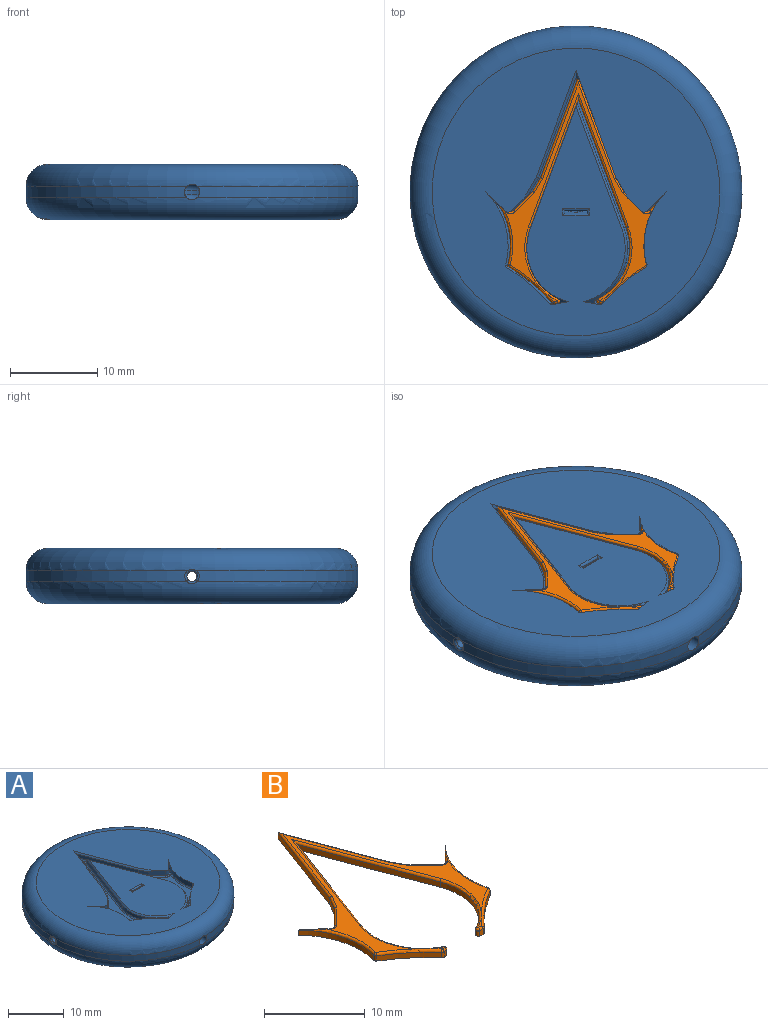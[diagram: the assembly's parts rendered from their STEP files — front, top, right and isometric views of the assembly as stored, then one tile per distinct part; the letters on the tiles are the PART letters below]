
ASSEMBLY  parts=2 mates=1
PART A: 133 faces, bbox 41.4x41.4x6.5 mm
  f0: cylinder r=19.05mm len=38.09mm, axis (0,0,-1), area 74.1mm2, adj f71,f72,f127,f131
  f1: cylinder r=19.05mm len=18.57mm, axis (0,0,-1), area 36mm2, adj f71,f72,f73,f126
  f2: cylinder r=2.31mm len=0.5mm, axis (0,0,1), area 0.1mm2, adj f92,f95,f97,f118
  f3: cylinder r=2.31mm len=0.5mm, axis (0,0,1), area 0.1mm2, adj f89,f95,f103,f111
  f4: cylinder r=0.57mm len=16.02mm, axis (1,0,0), area 56.8mm2, adj f105,f108,f109,f110,f111,f112,f125,f126
  f5: cylinder r=0.57mm len=16.02mm, axis (1,0,0), area 56.8mm2, adj f113,f116,f117,f118,f119,f120,f129,f130
  f6: plane 1.28x0.89mm, normal (0,0,1), area 0.2mm2, adj f49,f51,f54
  f7: plane 1.28x0.89mm, normal (0,0,1), area 0.2mm2, adj f60,f62,f65
  f8: plane 33.02x33.02mm, normal (0,0,1), area 758.2mm2, adj f10,f11,f12,f13,f18,f19,f20,f21
  f9: cylinder r=19.05mm len=18.57mm, axis (0,0,-1), area 36mm2, adj f71,f72,f73,f130
  f10: plane 2.17x2.17mm, normal (-0.71,-0.71,0), area 3.1mm2, adj f8,f11,f29,f61
  f11: cylinder r=8.72mm len=8.39mm, axis (0,0,1), area 9.2mm2, adj f8,f10,f35,f64
  f12: cylinder r=19.61mm len=4.97mm, axis (0,0,1), area 6.6mm2, adj f8,f35,f36,f65
  f13: plane 2.06x1.13mm, normal (-0.16,0.99,0), area 1mm2, adj f8,f34,f36,f37,f60
  f14: cylinder r=6.59mm len=8.22mm, axis (0,0,1), area 7.4mm2, adj f15,f34,f37,f62
  f15: plane 14.68x5.49mm, normal (-0.94,0.35,0), area 11.9mm2, adj f14,f16,f33,f58
  f16: plane 14.68x5.49mm, normal (0.94,0.35,0), area 11.9mm2, adj f15,f17,f32,f56
  f17: cylinder r=6.59mm len=8.22mm, axis (0,0,1), area 7.4mm2, adj f16,f31,f38,f54
  f18: plane 2.06x1.13mm, normal (0.16,0.99,0), area 1mm2, adj f8,f31,f38,f39,f49
  f19: cylinder r=19.61mm len=4.97mm, axis (0,0,1), area 6.6mm2, adj f8,f39,f40,f51
  f20: cylinder r=8.72mm len=8.39mm, axis (0,0,1), area 9.2mm2, adj f8,f21,f40,f45
  f21: plane 2.17x2.17mm, normal (0.71,-0.71,0), area 3.1mm2, adj f8,f20,f22,f43
  f22: cylinder r=0.53mm len=1.02mm, axis (0,0,1), area 0.8mm2, adj f8,f21,f23,f41
  f23: plane 2.17x2.17mm, normal (-0.71,-0.71,0), area 3mm2, adj f8,f22,f24,f42,f67
  f24: plane 1.58x0.92mm, normal (-0.86,-0.5,0), area 1.4mm2, adj f23,f25,f44,f67
  f25: plane 11.6x4.33mm, normal (-0.94,-0.35,0), area 9.4mm2, adj f24,f26,f46,f68
  f26: plane 11.6x4.33mm, normal (0.94,-0.35,0), area 9.4mm2, adj f25,f27,f50,f70
  f27: plane 1.58x0.92mm, normal (0.86,-0.5,0), area 1.4mm2, adj f26,f28,f53,f69
  f28: plane 2.17x2.17mm, normal (0.71,-0.71,0), area 3mm2, adj f8,f27,f29,f55,f69
  f29: cylinder r=0.53mm len=1.02mm, axis (0,0,1), area 0.8mm2, adj f8,f10,f28,f57
  f30: plane 23.34x16.83mm, normal (0,0,1), area 44mm2, adj f41,f42,f43,f44,f45,f46,f50,f51
  f31: cone r=6.59mm half-angle=45deg, axis (0,0,-1), area 4.1mm2, adj f8,f17,f18,f32,f38
  f32: plane 14.77x5.49mm, normal (0.66,0.25,0.71), area 5.5mm2, adj f8,f16,f31,f33
  f33: plane 14.77x5.49mm, normal (-0.66,0.25,0.71), area 5.5mm2, adj f8,f15,f32,f34
  f34: cone r=6.33mm half-angle=45deg, axis (0,0,-1), area 4.1mm2, adj f8,f13,f14,f33,f37
  f35: cylinder r=0.25mm len=1.02mm, axis (0,0,-1), area 0.3mm2, adj f8,f11,f12,f66
  f36: cylinder r=0.25mm len=1.02mm, axis (0,0,1), area 0.3mm2, adj f8,f12,f13,f63
  f37: cylinder r=0.25mm len=0.76mm, axis (0,0,1), area 0.3mm2, adj f13,f14,f34,f59
  f38: cylinder r=0.25mm len=0.76mm, axis (0,0,1), area 0.3mm2, adj f17,f18,f31,f52
  f39: cylinder r=0.25mm len=1.02mm, axis (0,0,1), area 0.3mm2, adj f8,f18,f19,f48
  f40: cylinder r=0.25mm len=1.02mm, axis (0,0,-1), area 0.3mm2, adj f8,f19,f20,f47
  f41: torus R=0.78mm, axis (0,0,1), area 0.4mm2, adj f22,f30,f42,f43
  f42: cylinder r=0.25mm len=2.37mm, axis (-0.71,0.71,0), area 1.2mm2, adj f23,f30,f41,f44
  f43: cylinder r=0.25mm len=2.35mm, axis (-0.71,-0.71,0), area 0.6mm2, adj f21,f30,f41,f45
  f44: cylinder r=0.25mm len=1.75mm, axis (-0.5,0.86,0), area 0.7mm2, adj f24,f30,f42,f46
  f45: torus R=8.97mm, axis (0,0,1), area 3.1mm2, adj f20,f30,f43,f47
  f46: cylinder r=0.25mm len=11.71mm, axis (-0.35,0.94,0), area 4.8mm2, adj f25,f30,f44,f50
  f47: sphere r=0.25mm, area 0.1mm2, adj f40,f45,f51
  f48: sphere r=0.25mm, area 0.1mm2, adj f39,f49,f51
  f49: cylinder r=0.25mm len=0.51mm, axis (0.99,-0.16,0), area 0.2mm2, adj f6,f18,f48,f52
  f50: cylinder r=0.25mm len=11.71mm, axis (-0.35,-0.94,0), area 4.8mm2, adj f26,f30,f46,f53
  f51: torus R=19.87mm, axis (0,0,1), area 2.6mm2, adj f6,f19,f30,f47,f48,f54
  f52: sphere r=0.25mm, area 0.2mm2, adj f38,f49,f54
  f53: cylinder r=0.25mm len=1.75mm, axis (-0.5,-0.86,0), area 0.7mm2, adj f27,f30,f50,f55
  f54: torus R=6.84mm, axis (0,0,1), area 3.9mm2, adj f6,f17,f30,f51,f52,f56
  f55: cylinder r=0.25mm len=2.37mm, axis (-0.71,-0.71,0), area 1.2mm2, adj f28,f30,f53,f57
  f56: cylinder r=0.25mm len=15.41mm, axis (0.35,-0.94,0), area 6.4mm2, adj f16,f30,f54,f58
  f57: torus R=0.78mm, axis (0,0,1), area 0.4mm2, adj f29,f30,f55,f61
  f58: cylinder r=0.25mm len=15.41mm, axis (0.35,0.94,0), area 6.4mm2, adj f15,f30,f56,f62
  f59: sphere r=0.25mm, area 0.1mm2, adj f37,f60,f62
  f60: cylinder r=0.25mm len=0.51mm, axis (0.99,0.16,0), area 0.2mm2, adj f7,f13,f59,f63
  f61: cylinder r=0.25mm len=2.35mm, axis (-0.71,0.71,0), area 0.6mm2, adj f10,f30,f57,f64
  f62: torus R=6.84mm, axis (0,0,1), area 3.9mm2, adj f7,f14,f30,f58,f59,f65
  f63: sphere r=0.25mm, area 0.1mm2, adj f36,f60,f65
  f64: torus R=8.97mm, axis (0,0,1), area 3.1mm2, adj f11,f30,f61,f66
  f65: torus R=19.87mm, axis (0,0,1), area 2.6mm2, adj f7,f12,f30,f62,f63,f66
  f66: sphere r=0.25mm, area 0.1mm2, adj f35,f64,f65
  f67: plane 2.4x1.63mm, normal (-0.61,-0.36,0.71), area 0.8mm2, adj f8,f23,f24,f68
  f68: plane 12.32x4.56mm, normal (-0.66,-0.25,0.71), area 4.6mm2, adj f8,f25,f67,f70
  f69: plane 2.4x1.63mm, normal (0.61,-0.36,0.71), area 0.8mm2, adj f8,f27,f28,f70
  f70: plane 12.32x4.56mm, normal (0.66,-0.25,0.71), area 4.6mm2, adj f8,f26,f68,f69
  f71: torus R=16.51mm, axis (0,0,1), area 453.9mm2, adj f0,f1,f9,f73,f87,f128,f129
  f72: torus R=16.51mm, axis (0,0,1), area 454mm2, adj f0,f1,f8,f9,f73,f125,f132
  f73: cylinder r=0.89mm len=16.69mm, axis (0,-1,0), area 85.5mm2, adj f1,f9,f71,f72,f77,f96,f97,f98
  f74: cylinder r=2.31mm len=3.97mm, axis (0,0,1), area 2.4mm2, adj f93,f95,f110,f119
  f75: plane 3.56x3.28mm, normal (0,0,-1), area 9.6mm2, adj f82,f83,f84,f95
  f76: plane 3.69x3.47mm, normal (0,0,1), area 8.7mm2, adj f89,f90,f91,f92,f93,f94
  f77: cylinder r=0.51mm len=2.54mm, axis (1,0,0), area 1.2mm2, adj f73,f78,f79,f83,f84,f85,f96,f104
  f78: plane 0.19x0.13mm, normal (0,0.24,0.97), area 0mm2, adj f77,f80,f83,f96
  f79: plane 0.19x0.13mm, normal (0,0.24,0.97), area 0mm2, adj f77,f81,f84,f104
  f80: plane 0.07x0.05mm, normal (0,0,1), area 0mm2, adj f78,f83,f96
  f81: plane 0.07x0.05mm, normal (0,0,1), area 0mm2, adj f79,f84,f104
  f82: cylinder r=0.51mm len=2.54mm, axis (1,0,0), area 1.4mm2, adj f75,f83,f84,f86
  f83: plane 2.34x1.46mm, normal (-1,0,0), area 0.7mm2, adj f75,f77,f78,f80,f82,f85,f86,f95
  f84: plane 2.34x1.46mm, normal (1,0,0), area 0.7mm2, adj f75,f77,f79,f81,f82,f85,f86,f95
  f85: plane 2.54x1.76mm, normal (0,1,0), area 4.5mm2, adj f77,f83,f84,f124
  f86: plane 2.54x1.58mm, normal (0,-1,0), area 4mm2, adj f82,f83,f84,f121
  f87: cylinder r=16.51mm len=33.02mm, axis (0,0,1), area 131.7mm2, adj f71,f88
  f88: plane 33.02x33.02mm, normal (0,0,-1), area 856.3mm2, adj f87
  f89: torus R=1.64mm, axis (0,0,1), area 1mm2, adj f3,f76,f90,f91,f102,f109
  f90: bspline ~1.73x0.82mm, area 0.2mm2, adj f76,f89,f92,f99,f100,f101
  f91: bspline ~1.08x0.73mm, area 0.4mm2, adj f76,f89,f93,f105,f106,f107
  f92: torus R=1.64mm, axis (0,0,1), area 1mm2, adj f2,f76,f90,f94,f98,f116
  f93: torus R=1.64mm, axis (0,0,1), area 5.4mm2, adj f74,f76,f91,f94,f108,f117
  f94: bspline ~1.08x0.73mm, area 0.4mm2, adj f76,f92,f93,f113,f114,f115
  f95: torus R=1.64mm, axis (0,0,1), area 7.6mm2, adj f2,f3,f74,f75,f83,f84,f96,f104
  f96: bspline ~3.04x1.8mm, area 2.7mm2, adj f73,f77,f78,f80,f83,f95,f97
  f97: bspline ~3.16x1.78mm, area 0.9mm2, adj f2,f73,f96,f98
  f98: bspline ~3.05x1.76mm, area 3.1mm2, adj f73,f92,f97,f99
  f99: bspline ~1.21x0.49mm, area 0.1mm2, adj f90,f98,f100
  f100: bspline ~0.82x0.48mm, area 0.3mm2, adj f73,f90,f99,f101
  f101: bspline ~1.29x0.58mm, area 0.3mm2, adj f73,f90,f100,f102
  f102: bspline ~3.05x1.76mm, area 3mm2, adj f73,f89,f101,f103
  f103: bspline ~3.17x2.53mm, area 0.9mm2, adj f3,f73,f102,f104
  f104: bspline ~3.04x1.8mm, area 2.7mm2, adj f73,f77,f79,f81,f84,f95,f103
  f105: bspline ~0.74x0.66mm, area 0.3mm2, adj f4,f91,f106,f107
  f106: bspline ~0.8x0.25mm, area 0mm2, adj f91,f105,f108
  f107: bspline ~0.8x0.25mm, area 0mm2, adj f91,f105,f109
  f108: bspline ~1.11x1.02mm, area 0.8mm2, adj f4,f93,f106,f110
  f109: bspline ~1.12x1.03mm, area 0.8mm2, adj f4,f89,f107,f111
  f110: bspline ~1.15x0.99mm, area 0.4mm2, adj f4,f74,f108,f112
  f111: bspline ~1.16x0.99mm, area 0.4mm2, adj f3,f4,f109,f112
  f112: bspline ~2.38x1.13mm, area 2.1mm2, adj f4,f95,f110,f111
  f113: bspline ~0.74x0.66mm, area 0.3mm2, adj f5,f94,f114,f115
  f114: bspline ~0.8x0.25mm, area 0mm2, adj f94,f113,f116
  f115: bspline ~0.8x0.25mm, area 0mm2, adj f94,f113,f117
  f116: bspline ~1.12x1.03mm, area 0.8mm2, adj f5,f92,f114,f118
  f117: bspline ~1.11x1.02mm, area 0.8mm2, adj f5,f93,f115,f119
  f118: bspline ~1.15x0.99mm, area 0.4mm2, adj f2,f5,f116,f120
  f119: bspline ~1.16x0.99mm, area 0.4mm2, adj f5,f74,f117,f120
  f120: bspline ~2.38x1.13mm, area 2.1mm2, adj f5,f95,f118,f119
  f121: cylinder r=0.25mm len=3.05mm, axis (1,0,0), area 1.1mm2, adj f8,f86,f122,f123
  f122: cylinder r=0.25mm len=0.76mm, axis (0,1,0), area 0.2mm2, adj f8,f84,f121,f124
  f123: cylinder r=0.25mm len=0.76mm, axis (0,-1,0), area 0.2mm2, adj f8,f83,f121,f124
  f124: cylinder r=0.25mm len=3.05mm, axis (-1,0,0), area 1.1mm2, adj f8,f85,f122,f123
  f125: bspline ~1.12x0.46mm, area 0.3mm2, adj f4,f72,f126,f127
  f126: bspline ~1.44x0.61mm, area 0.5mm2, adj f1,f4,f125,f128
  f127: bspline ~1.37x0.57mm, area 0.5mm2, adj f0,f4,f125,f128
  f128: bspline ~1.32x0.56mm, area 0.4mm2, adj f4,f71,f126,f127
  f129: bspline ~1.32x0.56mm, area 0.4mm2, adj f5,f71,f130,f131
  f130: bspline ~1.45x0.6mm, area 0.5mm2, adj f5,f9,f129,f132
  f131: bspline ~1.37x0.56mm, area 0.5mm2, adj f0,f5,f129,f132
  f132: bspline ~1.12x0.46mm, area 0.3mm2, adj f5,f72,f130,f131
PART B: 56 faces, bbox 21x26.4x0.9 mm
  f0: plane 1.23x0.89mm, normal (0,0,1), area 0.2mm2, adj f34,f35,f37,f51,f53
  f1: plane 1.23x0.89mm, normal (0,0,1), area 0.2mm2, adj f25,f26,f28,f47,f49
  f2: plane 23.34x16.83mm, normal (0,0,1), area 44mm2, adj f24,f25,f27,f28,f29,f30,f31,f32
  f3: cylinder r=19.61mm len=4.95mm, axis (0,0,1), area 4.1mm2, adj f23,f37,f52,f54
  f4: plane 0.64x0.38mm, normal (0.16,-0.99,0), area 0.2mm2, adj f23,f35,f50,f52
  f5: cylinder r=6.59mm len=8.19mm, axis (0,0,1), area 6.1mm2, adj f6,f23,f34,f50
  f6: plane 14.68x5.49mm, normal (0.94,-0.35,0), area 10mm2, adj f5,f7,f23,f32
  f7: plane 14.68x5.49mm, normal (-0.94,-0.35,0), area 10mm2, adj f6,f8,f23,f30
  f8: cylinder r=6.59mm len=8.19mm, axis (0,0,1), area 6.1mm2, adj f7,f23,f28,f48
  f9: plane 0.64x0.38mm, normal (-0.16,-0.99,0), area 0.2mm2, adj f23,f26,f46,f48
  f10: cylinder r=19.61mm len=4.95mm, axis (0,0,1), area 4.1mm2, adj f23,f25,f44,f46
  f11: cylinder r=8.72mm len=8.38mm, axis (0,0,1), area 5.8mm2, adj f12,f23,f24,f44
  f12: plane 2.17x2.17mm, normal (-0.71,0.71,0), area 2mm2, adj f11,f13,f23,f27
  f13: cylinder r=0.53mm len=0.75mm, axis (0,0,1), area 0.5mm2, adj f12,f14,f23,f29
  f14: plane 2.17x2.17mm, normal (0.71,0.71,0), area 1.9mm2, adj f13,f15,f23,f31
  f15: plane 1.58x0.92mm, normal (0.86,0.5,0), area 1.2mm2, adj f14,f16,f23,f33
  f16: plane 11.6x4.33mm, normal (0.94,0.35,0), area 7.9mm2, adj f15,f17,f23,f36
  f17: plane 11.6x4.33mm, normal (-0.94,0.35,0), area 7.9mm2, adj f16,f18,f23,f38
  f18: plane 1.58x0.92mm, normal (-0.86,0.5,0), area 1.2mm2, adj f17,f19,f23,f40
  f19: plane 2.17x2.17mm, normal (-0.71,0.71,0), area 1.9mm2, adj f18,f20,f23,f42
  f20: cylinder r=0.53mm len=0.75mm, axis (0,0,1), area 0.5mm2, adj f19,f21,f23,f43
  f21: plane 2.17x2.17mm, normal (0.71,0.71,0), area 2mm2, adj f20,f22,f23,f41
  f22: cylinder r=8.72mm len=8.38mm, axis (0,0,1), area 5.8mm2, adj f21,f23,f39,f54
  f23: plane 26.1x20.68mm, normal (0,0,-1), area 74.7mm2, adj f3,f4,f5,f6,f7,f8,f9,f10
  f24: torus R=8.97mm, axis (0,0,1), area 3mm2, adj f2,f11,f27,f45
  f25: torus R=19.87mm, axis (0,0,1), area 2.6mm2, adj f1,f2,f10,f28,f45,f47
  f26: cylinder r=0.25mm len=0.42mm, axis (0.99,-0.16,0), area 0.2mm2, adj f1,f9,f47,f49
  f27: cylinder r=0.25mm len=2.35mm, axis (-0.71,-0.71,0), area 0.6mm2, adj f2,f12,f24,f29
  f28: torus R=6.84mm, axis (0,0,1), area 3.9mm2, adj f1,f2,f8,f25,f30,f49
  f29: torus R=0.78mm, axis (0,0,1), area 0.4mm2, adj f2,f13,f27,f31
  f30: cylinder r=0.25mm len=15.41mm, axis (0.35,-0.94,0), area 6.4mm2, adj f2,f7,f28,f32
  f31: cylinder r=0.25mm len=2.37mm, axis (-0.71,0.71,0), area 1.2mm2, adj f2,f14,f29,f33
  f32: cylinder r=0.25mm len=15.41mm, axis (0.35,0.94,0), area 6.4mm2, adj f2,f6,f30,f34
  f33: cylinder r=0.25mm len=1.75mm, axis (-0.5,0.86,0), area 0.7mm2, adj f2,f15,f31,f36
  f34: torus R=6.84mm, axis (0,0,1), area 3.9mm2, adj f0,f2,f5,f32,f37,f51
  f35: cylinder r=0.25mm len=0.42mm, axis (0.99,0.16,0), area 0.2mm2, adj f0,f4,f51,f53
  f36: cylinder r=0.25mm len=11.71mm, axis (-0.35,0.94,0), area 4.8mm2, adj f2,f16,f33,f38
  f37: torus R=19.87mm, axis (0,0,1), area 2.6mm2, adj f0,f2,f3,f34,f53,f55
  f38: cylinder r=0.25mm len=11.71mm, axis (-0.35,-0.94,0), area 4.8mm2, adj f2,f17,f36,f40
  f39: torus R=8.97mm, axis (0,0,1), area 3mm2, adj f2,f22,f41,f55
  f40: cylinder r=0.25mm len=1.75mm, axis (-0.5,-0.86,0), area 0.7mm2, adj f2,f18,f38,f42
  f41: cylinder r=0.25mm len=2.35mm, axis (-0.71,0.71,0), area 0.6mm2, adj f2,f21,f39,f43
  f42: cylinder r=0.25mm len=2.37mm, axis (-0.71,-0.71,0), area 1.2mm2, adj f2,f19,f40,f43
  f43: torus R=0.78mm, axis (0,0,1), area 0.4mm2, adj f2,f20,f41,f42
  f44: cylinder r=0.28mm len=0.64mm, axis (0,0,1), area 0.2mm2, adj f10,f11,f23,f45
  f45: torus R=0.03mm, axis (0,0,1), area 0.1mm2, adj f2,f24,f25,f44
  f46: cylinder r=0.28mm len=0.64mm, axis (0,0,1), area 0.2mm2, adj f9,f10,f23,f47
  f47: torus R=0.03mm, axis (0,0,1), area 0.1mm2, adj f1,f25,f26,f46
  f48: cylinder r=0.28mm len=0.64mm, axis (0,0,1), area 0.4mm2, adj f8,f9,f23,f49
  f49: torus R=0.03mm, axis (0,0,1), area 0.2mm2, adj f1,f26,f28,f48
  f50: cylinder r=0.28mm len=0.64mm, axis (0,0,1), area 0.4mm2, adj f4,f5,f23,f51
  f51: torus R=0.03mm, axis (0,0,1), area 0.2mm2, adj f0,f34,f35,f50
  f52: cylinder r=0.28mm len=0.64mm, axis (0,0,1), area 0.2mm2, adj f3,f4,f23,f53
  f53: torus R=0.03mm, axis (0,0,1), area 0.1mm2, adj f0,f35,f37,f52
  f54: cylinder r=0.28mm len=0.64mm, axis (0,0,1), area 0.2mm2, adj f3,f22,f23,f55
  f55: torus R=0.03mm, axis (0,0,1), area 0.1mm2, adj f2,f37,f39,f54
PLACE A t=(-7.48,-1.77,0.62)mm
PLACE B t=(20.82,-35.41,6.08)mm
MATE planar B.f44 <-> A.f8  axis (0,0,1) through (0.59,-10.16,6.97)mm
